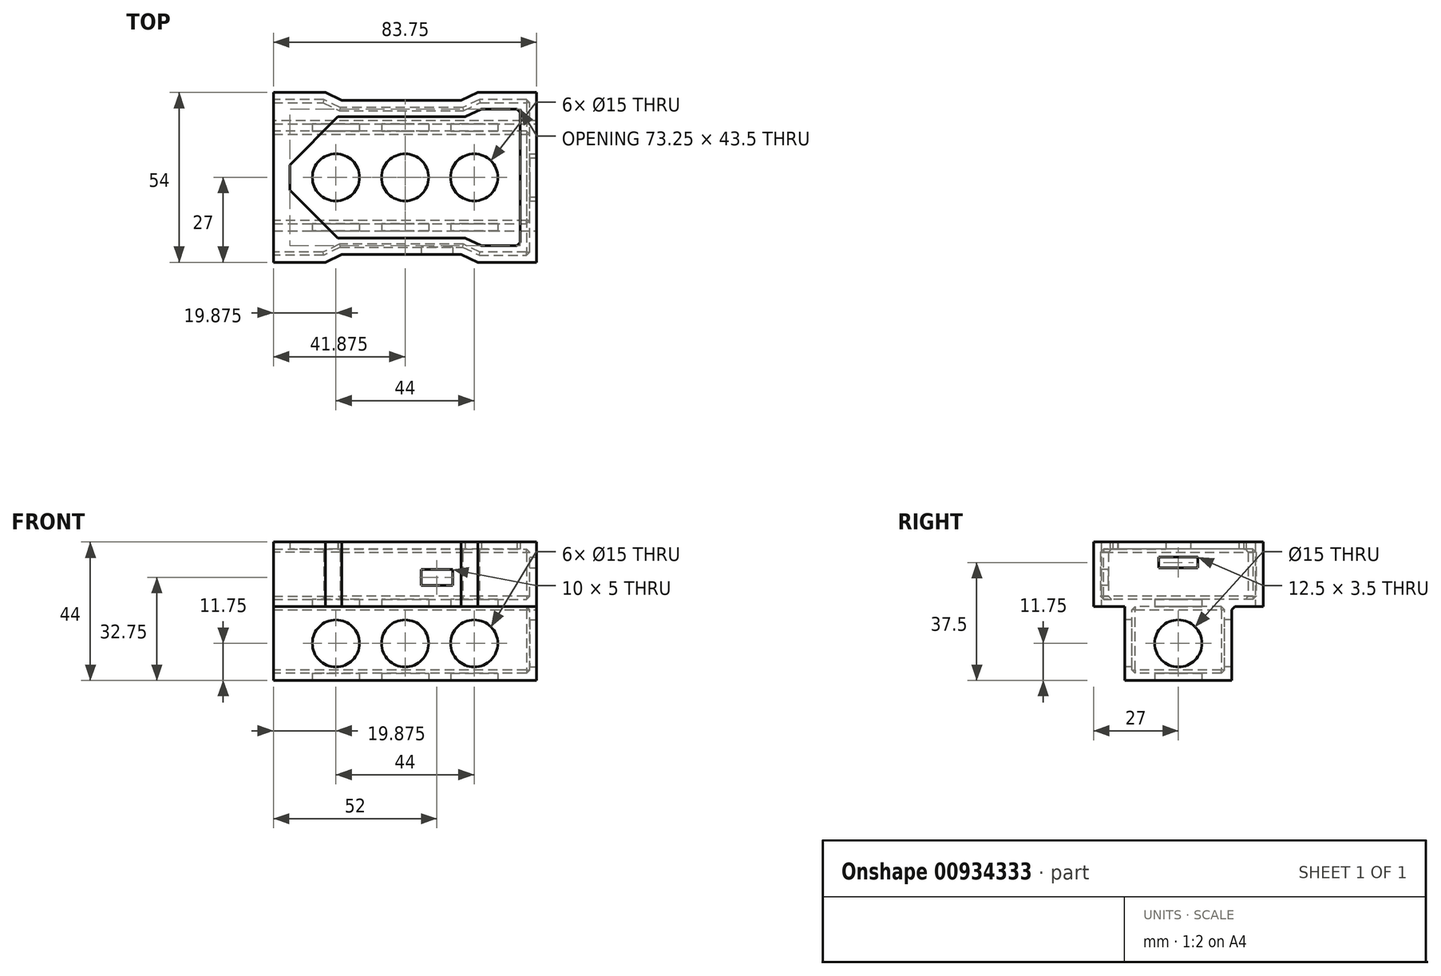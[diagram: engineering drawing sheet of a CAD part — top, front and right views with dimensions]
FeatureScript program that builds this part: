
annotation { "Feature Type Name" : "Feature", "Feature Type Description" : "" }
export const myFeature = defineFeature(function(context is Context, id is Id, definition is map)
    precondition{}
    {
        {
            var Q0;
            Q0=qCreatedBy(makeId("Top.planeOp"),FACE);
            var sketch = newSketch(context, id + "F0", { "sketchPlane" : qUnion([Q0])});
            skLineSegment(sketch, "E0.bottom", {"start": v(0, 0) * mm, "end": v(16, 0) * mm});
            skLineSegment(sketch, "E0.left", {"start": v(0, 0) * mm, "end": v(0, 24.75) * mm});
            skLineSegment(sketch, "E0.right", {"start": v(81.5, 0) * mm, "end": v(81.5, 24.75) * mm});
            skLineSegment(sketch, "E1", {"start": v(16, 0) * mm, "end": v(21.25, 2.5) * mm});
            skLineSegment(sketch, "E2", {"start": v(21.25, 2.5) * mm, "end": v(60.25, 2.5) * mm});
            skLineSegment(sketch, "E3", {"start": v(60.25, 2.5) * mm, "end": v(65.5, 0) * mm});
            skLineSegment(sketch, "E4.trimOffspring", {"start": v(65.5, 0) * mm, "end": v(81.5, 0) * mm});
            skLineSegment(sketch, "E5", {"start": v(0, 24.75) * mm, "end": v(81.5, 24.75) * mm, "construction": true});
            skLineSegment(sketch, "E6.MirrorCS", {"start": v(0, 49.5) * mm, "end": v(0, 24.75) * mm});
            skLineSegment(sketch, "E7.MirrorCS", {"start": v(60.25, 47) * mm, "end": v(65.5, 49.5) * mm});
            skLineSegment(sketch, "E8.MirrorCS", {"start": v(81.5, 49.5) * mm, "end": v(81.5, 24.75) * mm});
            skLineSegment(sketch, "E9.MirrorCS", {"start": v(65.5, 49.5) * mm, "end": v(81.5, 49.5) * mm});
            skLineSegment(sketch, "E10.MirrorCS", {"start": v(16, 49.5) * mm, "end": v(21.25, 47) * mm});
            skLineSegment(sketch, "E11.MirrorCS", {"start": v(21.25, 47) * mm, "end": v(60.25, 47) * mm});
            skLineSegment(sketch, "E12.MirrorCS", {"start": v(0, 49.5) * mm, "end": v(16, 49.5) * mm});
            skSolve(sketch);
        }
        {
            var Q0;
            Q0=makeQuery(id+"F0.imprint","IMPRINT",FACE,{"disambiguationData":[TD([[makeQuery(id+"F0.imprint","IMPRINT",EDGE,{"derivedFrom":sQuery(id+"F0.wireOp",EDGE,"E0.bottom")}),1.0]])]});
            extrude(context, id + "F1", {"entities" : qUnion([Q0]), "depth" : 16 * mm, "offsetDistance" : 25 * mm});
        }
        {
            var Q0;
            Q0=makeQuery(id+"F1.opExtrude","SWEPT_FACE",FACE,{"disambiguationData":[OSD([sQuery(id+"F0.wireOp",EDGE,"E0.left"),sQuery(id+"F0.wireOp",EDGE,"E6.MirrorCS")])]});
            shell(context, id + "F2", {"entities" : qUnion([Q0]), "thickness" : 2.25 * mm, "oppositeDirection" : true});
        }
        {
            var Q0;
            Q0=makeQuery(id+"F1.opExtrude","CAP_FACE",FACE,{"disambiguationData":[OSD([sQuery(id+"F0.wireOp",EDGE,"E0.bottom"),sQuery(id+"F0.wireOp",EDGE,"E0.left"),sQuery(id+"F0.wireOp",EDGE,"E0.right"),sQuery(id+"F0.wireOp",EDGE,"E1"),sQuery(id+"F0.wireOp",EDGE,"E2"),sQuery(id+"F0.wireOp",EDGE,"E3"),sQuery(id+"F0.wireOp",EDGE,"E4.trimOffspring"),sQuery(id+"F0.wireOp",EDGE,"E6.MirrorCS"),sQuery(id+"F0.wireOp",EDGE,"E7.MirrorCS"),sQuery(id+"F0.wireOp",EDGE,"E8.MirrorCS"),sQuery(id+"F0.wireOp",EDGE,"E9.MirrorCS"),sQuery(id+"F0.wireOp",EDGE,"E10.MirrorCS"),sQuery(id+"F0.wireOp",EDGE,"E11.MirrorCS"),sQuery(id+"F0.wireOp",EDGE,"E12.MirrorCS")])],"isStart":true});
            var sketch = newSketch(context, id + "F3", { "sketchPlane" : qUnion([Q0])});
            skLineSegment(sketch, "E13.bottom", {"start": v(0, -7.75) * mm, "end": v(83.75, -7.75) * mm});
            skLineSegment(sketch, "E13.top", {"start": v(0, -41.75) * mm, "end": v(83.75, -41.75) * mm});
            skLineSegment(sketch, "E13.left", {"start": v(0, -7.75) * mm, "end": v(0, -41.75) * mm});
            skLineSegment(sketch, "E13.right", {"start": v(83.75, -7.75) * mm, "end": v(83.75, -41.75) * mm});
            skPoint(sketch, "E14", {"position": v(0, -24.75) * mm});
            skSolve(sketch);
        }
        {
            var Q0;
            Q0 = qSketchRegion(id + "F3", true);
            extrude(context, id + "F4", {"entities" : qUnion([Q0]), "operationType" : NewBodyOperationType.ADD, "depth" : 23.5 * mm, "offsetDistance" : 25 * mm});
        }
        {
            var Q0;
            Q0=makeQuery(id+"F4.boolean.opBoolean","MERGE",FACE,{"derivedFrom":[makeQuery(id+"F1.opExtrude","SWEPT_FACE",FACE,{"disambiguationData":[OSD([sQuery(id+"F0.wireOp",EDGE,"bd4c0ab3-f638-437a-942f-3d293cf75bfd.9"),sQuery(id+"F0.wireOp",EDGE,"bd4c0ab3-f638-437a-942f-3d293cf75bfd.11")])]}),makeQuery(id+"F4.opExtrude","SWEPT_FACE",FACE,{"disambiguationData":[OSD([sQuery(id+"Filse6hUhfh3Ufs_1.wireOp",EDGE,"bbtqiL3y-JQfm-Av7l-CrqV-hF6hky0nlNgT.left")])]})]});
            var Q1;
            Q1=makeQuery(id+"F4.boolean.opBoolean","MERGE",FACE,{"derivedFrom":[makeQuery(id+"F1.opExtrude","SWEPT_FACE",FACE,{"disambiguationData":[OSD([sQuery(id+"F0.wireOp",EDGE,"E0.left"),sQuery(id+"F0.wireOp",EDGE,"E6.MirrorCS")])]}),makeQuery(id+"F4.opExtrude","SWEPT_FACE",FACE,{"disambiguationData":[OSD([sQuery(id+"F3.wireOp",EDGE,"E13.left")])]})]});
            var Q2;
            Q2=makeQuery(id+"F1.opExtrude","SWEPT_BODY",BODY,{"disambiguationData":[OSD([sQuery(id+"F0.wireOp",EDGE,"E0.bottom"),sQuery(id+"F0.wireOp",EDGE,"E0.left"),sQuery(id+"F0.wireOp",EDGE,"E0.right"),sQuery(id+"F0.wireOp",EDGE,"E1"),sQuery(id+"F0.wireOp",EDGE,"E2"),sQuery(id+"F0.wireOp",EDGE,"E3"),sQuery(id+"F0.wireOp",EDGE,"E4.trimOffspring"),sQuery(id+"F0.wireOp",EDGE,"E6.MirrorCS"),sQuery(id+"F0.wireOp",EDGE,"E7.MirrorCS"),sQuery(id+"F0.wireOp",EDGE,"E8.MirrorCS"),sQuery(id+"F0.wireOp",EDGE,"E9.MirrorCS"),sQuery(id+"F0.wireOp",EDGE,"E10.MirrorCS"),sQuery(id+"F0.wireOp",EDGE,"E11.MirrorCS"),sQuery(id+"F0.wireOp",EDGE,"E12.MirrorCS")])]});
            shell(context, id + "F5", {"entities" : qUnion([Q0, Q1]), "parts" : qUnion([Q2]), "thickness" : 2.25 * mm});
        }
        {
            var Q0;
            {var subQ0=sQuery(id+"F0.wireOp",EDGE,"E12.MirrorCS");var subQ1=sQuery(id+"F0.wireOp",EDGE,"E11.MirrorCS");var subQ2=sQuery(id+"F0.wireOp",EDGE,"E10.MirrorCS");var subQ3=sQuery(id+"F0.wireOp",EDGE,"E9.MirrorCS");var subQ4=sQuery(id+"F0.wireOp",EDGE,"E8.MirrorCS");var subQ5=sQuery(id+"F0.wireOp",EDGE,"E7.MirrorCS");var subQ6=sQuery(id+"F0.wireOp",EDGE,"E6.MirrorCS");var subQ7=sQuery(id+"F0.wireOp",EDGE,"E4.trimOffspring");var subQ8=sQuery(id+"F0.wireOp",EDGE,"E3");var subQ9=sQuery(id+"F0.wireOp",EDGE,"E2");var subQ10=sQuery(id+"F0.wireOp",EDGE,"E1");var subQ11=sQuery(id+"F0.wireOp",EDGE,"E0.right");var subQ12=sQuery(id+"F0.wireOp",EDGE,"E0.left");var subQ13=sQuery(id+"F0.wireOp",EDGE,"E0.bottom");Q0=makeQuery(id+"F2.opShell","OFFSET_FACE",FACE,{"disambiguationData":[OSD([subQ13,subQ12,subQ11,subQ10,subQ9,subQ8,subQ7,subQ6,subQ5,subQ4,subQ3,subQ2,subQ1,subQ0]),TDD([makeQuery(id+"F1.opExtrude","CAP_FACE",FACE,{"disambiguationData":[OSD([subQ13,subQ12,subQ11,subQ10,subQ9,subQ8,subQ7,subQ6,subQ5,subQ4,subQ3,subQ2,subQ1,subQ0])],"isStart":false})])]});}
            var Q1;
            Q1=makeQuery(id+"F1.opExtrude","CAP_FACE",FACE,{"disambiguationData":[OSD([sQuery(id+"F0.wireOp",EDGE,"E0.bottom"),sQuery(id+"F0.wireOp",EDGE,"E0.left"),sQuery(id+"F0.wireOp",EDGE,"E0.right"),sQuery(id+"F0.wireOp",EDGE,"E1"),sQuery(id+"F0.wireOp",EDGE,"E2"),sQuery(id+"F0.wireOp",EDGE,"E3"),sQuery(id+"F0.wireOp",EDGE,"E4.trimOffspring"),sQuery(id+"F0.wireOp",EDGE,"E6.MirrorCS"),sQuery(id+"F0.wireOp",EDGE,"E7.MirrorCS"),sQuery(id+"F0.wireOp",EDGE,"E8.MirrorCS"),sQuery(id+"F0.wireOp",EDGE,"E9.MirrorCS"),sQuery(id+"F0.wireOp",EDGE,"E10.MirrorCS"),sQuery(id+"F0.wireOp",EDGE,"E11.MirrorCS"),sQuery(id+"F0.wireOp",EDGE,"E12.MirrorCS")])],"isStart":false});
            shell(context, id + "F6", {"entities" : qUnion([Q0, Q1]), "thickness" : 5.25 * mm});
        }
        {
            var Q0;
            Q0=makeQuery(id+"F6.opShell","OFFSET_EDGE",EDGE,{"disambiguationData":[OSD([sQuery(id+"F0.wireOp",EDGE,"E6.MirrorCS"),sQuery(id+"F0.wireOp",EDGE,"E12.MirrorCS")])]});
            var Q1;
            Q1=makeQuery(id+"F6.opShell","OFFSET_EDGE",EDGE,{"disambiguationData":[OSD([sQuery(id+"F0.wireOp",EDGE,"E0.bottom"),sQuery(id+"F0.wireOp",EDGE,"E0.left")])]});
            chamfer(context, id + "F7", {"entities" : qUnion([Q0, Q1]), "width" : 17.75 * mm, "tangentPropagation" : true});
        }
        {
            var Q0;
            Q0=makeQuery(id+"F4.boolean.opBoolean","MERGE",FACE,{"derivedFrom":[makeQuery(id+"F1.opExtrude","SWEPT_FACE",FACE,{"disambiguationData":[OSD([sQuery(id+"F0.wireOp",EDGE,"E0.right"),sQuery(id+"F0.wireOp",EDGE,"E8.MirrorCS")])]}),makeQuery(id+"F4.opExtrude","SWEPT_FACE",FACE,{"disambiguationData":[OSD([sQuery(id+"F3.wireOp",EDGE,"E13.right")])]})]});
            var sketch = newSketch(context, id + "F8", { "sketchPlane" : qUnion([Q0])});
            skPoint(sketch, "E15", {"position": v(24.75, -14) * mm});
            skPoint(sketch, "E16", {"position": v(27.14, 12.96) * mm});
            skPoint(sketch, "E17", {"position": v(-220.52, 60.4) * mm});
            skPoint(sketch, "E18", {"position": v(-318.2, 70.36) * mm});
            skSolve(sketch);
        }
        {
            var Q0;
            Q0=makeQuery(id+"F4.opExtrude","SWEPT_FACE",FACE,{"disambiguationData":[OSD([sQuery(id+"F3.wireOp",EDGE,"E13.bottom")])]});
            var sketch = newSketch(context, id + "F9", { "sketchPlane" : qUnion([Q0])});
            skPoint(sketch, "E19", {"position": v(41.88, -14) * mm});
            skPoint(sketch, "E20", {"position": v(19.88, -14) * mm});
            skPoint(sketch, "E21", {"position": v(63.88, -14) * mm});
            skSolve(sketch);
        }
        {
            var Q0;
            Q0=makeQuery(id+"F4.opExtrude","CAP_FACE",FACE,{"disambiguationData":[OSD([sQuery(id+"F3.wireOp",EDGE,"E13.bottom"),sQuery(id+"F3.wireOp",EDGE,"E13.top"),sQuery(id+"F3.wireOp",EDGE,"E13.left"),sQuery(id+"F3.wireOp",EDGE,"E13.right")])],"isStart":false});
            var sketch = newSketch(context, id + "F10", { "sketchPlane" : qUnion([Q0])});
            skPoint(sketch, "E22", {"position": v(63.88, -24.75) * mm});
            skPoint(sketch, "E22.positionSnap0", {"position": v(83.75, -24.75) * mm});
            skPoint(sketch, "E23", {"position": v(41.88, -24.75) * mm});
            skPoint(sketch, "E24", {"position": v(19.88, -24.75) * mm});
            skSolve(sketch);
        }
        {
            var Q0;
            Q0=sQuery(id+"F8.wireOp",VERTEX,"E15");
            var Q1;
            Q1=sQuery(id+"F9.wireOp",VERTEX,"E19");
            var Q2;
            Q2=sQuery(id+"F9.wireOp",VERTEX,"E20");
            var Q3;
            Q3=sQuery(id+"F9.wireOp",VERTEX,"E21");
            var Q4;
            Q4=sQuery(id+"F10.wireOp",VERTEX,"E24");
            var Q5;
            Q5=sQuery(id+"F10.wireOp",VERTEX,"E23");
            var Q6;
            Q6=sQuery(id+"F10.wireOp",VERTEX,"E22");
            var Q7;
            Q7=makeQuery(id+"F1.opExtrude","SWEPT_BODY",BODY,{"disambiguationData":[OSD([sQuery(id+"F0.wireOp",EDGE,"E0.bottom"),sQuery(id+"F0.wireOp",EDGE,"E0.left"),sQuery(id+"F0.wireOp",EDGE,"E0.right"),sQuery(id+"F0.wireOp",EDGE,"E1"),sQuery(id+"F0.wireOp",EDGE,"E2"),sQuery(id+"F0.wireOp",EDGE,"E3"),sQuery(id+"F0.wireOp",EDGE,"E4.trimOffspring"),sQuery(id+"F0.wireOp",EDGE,"E6.MirrorCS"),sQuery(id+"F0.wireOp",EDGE,"E7.MirrorCS"),sQuery(id+"F0.wireOp",EDGE,"E8.MirrorCS"),sQuery(id+"F0.wireOp",EDGE,"E9.MirrorCS"),sQuery(id+"F0.wireOp",EDGE,"E10.MirrorCS"),sQuery(id+"F0.wireOp",EDGE,"E11.MirrorCS"),sQuery(id+"F0.wireOp",EDGE,"E12.MirrorCS")])]});
            hole(context, id + "F11", {"style" : HoleStyle.SIMPLE, "endStyle" : HoleEndStyle.BLIND, "holeDiameter" : 15 * mm, "majorDiameter" : 5 * mm, "holeDepth" : 300 * mm, "isTappedThrough" : true, "tappedDepth" : 12 * mm, "tapClearance" : 3, "startFromSketch" : true, "locations" : qUnion([Q0, Q1, Q2, Q3, Q4, Q5, Q6]), "scope" : qUnion([Q7])});
        }
        {
            var Q0;
            {var subQ0=sQuery(id+"F3.wireOp",EDGE,"E13.right");Q0=makeQuery(id+"F8.imprint","IMPRINT",FACE,{"disambiguationData":[TD([[makeQuery(id+"F8.imprint","IMPRINT",EDGE,{"derivedFrom":makeQuery(id+"F4.opExtrude","CAP_EDGE",EDGE,{"disambiguationData":[OSD([subQ0])],"isStart":false})}),1.0]])]});}
            var sketch = newSketch(context, id + "F12", { "sketchPlane" : qUnion([Q0])});
            skLineSegment(sketch, "E25.bottom", {"start": v(18.5, 13.5) * mm, "end": v(31, 13.5) * mm});
            skLineSegment(sketch, "E25.top", {"start": v(18.5, 10) * mm, "end": v(31, 10) * mm});
            skLineSegment(sketch, "E25.left", {"start": v(18.5, 13.5) * mm, "end": v(18.5, 10) * mm});
            skLineSegment(sketch, "E25.right", {"start": v(31, 13.5) * mm, "end": v(31, 10) * mm});
            skPoint(sketch, "E26", {"position": v(24.75, 13.5) * mm});
            skSolve(sketch);
        }
        {
            var Q0;
            Q0 = qSketchRegion(id + "F12", true);
            extrude(context, id + "F13", {"entities" : qUnion([Q0]), "operationType" : NewBodyOperationType.REMOVE, "oppositeDirection" : true, "depth" : 25 * mm, "offsetDistance" : 25 * mm});
        }
        {
            var Q0;
            Q0=makeQuery(id+"F1.opExtrude","SWEPT_FACE",FACE,{"disambiguationData":[OSD([sQuery(id+"F0.wireOp",EDGE,"E2")])]});
            var sketch = newSketch(context, id + "F14", { "sketchPlane" : qUnion([Q0])});
            skLineSegment(sketch, "E27.bottom", {"start": v(47, 9.5) * mm, "end": v(57, 9.5) * mm});
            skLineSegment(sketch, "E27.top", {"start": v(47, 4.5) * mm, "end": v(57, 4.5) * mm});
            skLineSegment(sketch, "E27.left", {"start": v(47, 9.5) * mm, "end": v(47, 4.5) * mm});
            skLineSegment(sketch, "E27.right", {"start": v(57, 9.5) * mm, "end": v(57, 4.5) * mm});
            skSolve(sketch);
        }
        {
            var Q0;
            Q0 = qSketchRegion(id + "F14", true);
            extrude(context, id + "F15", {"entities" : qUnion([Q0]), "operationType" : NewBodyOperationType.REMOVE, "oppositeDirection" : true, "depth" : 25 * mm, "offsetDistance" : 25 * mm});
        }
        {
            var Q0;
            Q0=makeQuery(id+"F5.opShell","OFFSET_EDGE",EDGE,{"disambiguationData":[OSD([sQuery(id+"F3.wireOp",EDGE,"E13.top")])]});
            var Q1;
            Q1=makeQuery(id+"F5.opShell","OFFSET_EDGE",EDGE,{"disambiguationData":[OSD([sQuery(id+"F3.wireOp",EDGE,"E13.bottom")])]});
            var Q2;
            Q2=makeQuery(id+"F4.opExtrude","CAP_EDGE",EDGE,{"disambiguationData":[OSD([sQuery(id+"F3.wireOp",EDGE,"E13.top")])],"isStart":true});
            var Q3;
            Q3=makeQuery(id+"F4.opExtrude","CAP_EDGE",EDGE,{"disambiguationData":[OSD([sQuery(id+"F3.wireOp",EDGE,"E13.bottom")])],"isStart":true});
            var Q4;
            Q4=makeQuery(id+"F5.opShell","OFFSET_EDGE",EDGE,{"disambiguationData":[OSD([sQuery(id+"F3.wireOp",EDGE,"E13.right")])]});
            var Q5;
            Q5=makeQuery(id+"F5.opShell","OFFSET_EDGE",EDGE,{"disambiguationData":[OSD([sQuery(id+"F0.wireOp",EDGE,"E0.right"),sQuery(id+"F0.wireOp",EDGE,"E8.MirrorCS"),sQuery(id+"F3.wireOp",EDGE,"E13.bottom"),sQuery(id+"F3.wireOp",EDGE,"E13.right")])]});
            var Q6;
            Q6=makeQuery(id+"F5.opShell","OFFSET_EDGE",EDGE,{"disambiguationData":[OSD([sQuery(id+"F0.wireOp",EDGE,"E0.right"),sQuery(id+"F0.wireOp",EDGE,"E8.MirrorCS"),sQuery(id+"F3.wireOp",EDGE,"E13.top"),sQuery(id+"F3.wireOp",EDGE,"E13.right")])]});
            var Q7;
            {var subQ0=sQuery(id+"F0.wireOp",EDGE,"E12.MirrorCS");var subQ1=sQuery(id+"F0.wireOp",EDGE,"E11.MirrorCS");var subQ2=sQuery(id+"F0.wireOp",EDGE,"E10.MirrorCS");var subQ3=sQuery(id+"F0.wireOp",EDGE,"E9.MirrorCS");var subQ4=sQuery(id+"F0.wireOp",EDGE,"E8.MirrorCS");var subQ5=sQuery(id+"F0.wireOp",EDGE,"E7.MirrorCS");var subQ6=sQuery(id+"F0.wireOp",EDGE,"E6.MirrorCS");var subQ7=sQuery(id+"F0.wireOp",EDGE,"E4.trimOffspring");var subQ8=sQuery(id+"F0.wireOp",EDGE,"E3");var subQ9=sQuery(id+"F0.wireOp",EDGE,"E2");var subQ10=sQuery(id+"F0.wireOp",EDGE,"E1");var subQ11=sQuery(id+"F0.wireOp",EDGE,"E0.right");var subQ12=sQuery(id+"F0.wireOp",EDGE,"E0.left");var subQ13=sQuery(id+"F0.wireOp",EDGE,"E0.bottom");Q7=makeQuery(id+"F5.opShell","TWEAK_EDGE",EDGE,{"derivedFrom":[makeQuery(id+"F2.opShell","OFFSET_FACE",FACE,{"disambiguationData":[OSD([subQ13,subQ12,subQ11,subQ10,subQ9,subQ8,subQ7,subQ6,subQ5,subQ4,subQ3,subQ2,subQ1,subQ0]),TDD([makeQuery(id+"F1.opExtrude","CAP_FACE",FACE,{"disambiguationData":[OSD([subQ13,subQ12,subQ11,subQ10,subQ9,subQ8,subQ7,subQ6,subQ5,subQ4,subQ3,subQ2,subQ1,subQ0])],"isStart":true})])]}),makeQuery(id+"F4.opExtrude","SWEPT_FACE",FACE,{"disambiguationData":[OSD([sQuery(id+"F3.wireOp",EDGE,"E13.top")])]})]});}
            var Q8;
            {var subQ0=sQuery(id+"F0.wireOp",EDGE,"E8.MirrorCS");var subQ1=sQuery(id+"F0.wireOp",EDGE,"E0.right");var subQ2=sQuery(id+"F0.wireOp",EDGE,"E12.MirrorCS");var subQ3=sQuery(id+"F0.wireOp",EDGE,"E11.MirrorCS");var subQ4=sQuery(id+"F0.wireOp",EDGE,"E10.MirrorCS");var subQ5=sQuery(id+"F0.wireOp",EDGE,"E9.MirrorCS");var subQ6=sQuery(id+"F0.wireOp",EDGE,"E7.MirrorCS");var subQ7=sQuery(id+"F0.wireOp",EDGE,"E6.MirrorCS");var subQ8=sQuery(id+"F0.wireOp",EDGE,"E4.trimOffspring");var subQ9=sQuery(id+"F0.wireOp",EDGE,"E3");var subQ10=sQuery(id+"F0.wireOp",EDGE,"E2");var subQ11=sQuery(id+"F0.wireOp",EDGE,"E1");var subQ12=sQuery(id+"F0.wireOp",EDGE,"E0.left");var subQ13=sQuery(id+"F0.wireOp",EDGE,"E0.bottom");Q8=makeQuery(id+"F5.opShell","TWEAK_EDGE",EDGE,{"derivedFrom":[makeQuery(id+"F2.opShell","OFFSET_FACE",FACE,{"disambiguationData":[OSD([subQ13,subQ12,subQ1,subQ11,subQ10,subQ9,subQ8,subQ7,subQ6,subQ0,subQ5,subQ4,subQ3,subQ2]),TDD([makeQuery(id+"F1.opExtrude","CAP_FACE",FACE,{"disambiguationData":[OSD([subQ13,subQ12,subQ1,subQ11,subQ10,subQ9,subQ8,subQ7,subQ6,subQ0,subQ5,subQ4,subQ3,subQ2])],"isStart":true})])]}),makeQuery(id+"F4.boolean.opBoolean","MERGE",FACE,{"derivedFrom":[makeQuery(id+"F1.opExtrude","SWEPT_FACE",FACE,{"disambiguationData":[OSD([subQ1,subQ0])]}),makeQuery(id+"F4.opExtrude","SWEPT_FACE",FACE,{"disambiguationData":[OSD([sQuery(id+"F3.wireOp",EDGE,"E13.right")])]})]})]});}
            var Q9;
            {var subQ0=sQuery(id+"F0.wireOp",EDGE,"E12.MirrorCS");var subQ1=sQuery(id+"F0.wireOp",EDGE,"E11.MirrorCS");var subQ2=sQuery(id+"F0.wireOp",EDGE,"E10.MirrorCS");var subQ3=sQuery(id+"F0.wireOp",EDGE,"E9.MirrorCS");var subQ4=sQuery(id+"F0.wireOp",EDGE,"E8.MirrorCS");var subQ5=sQuery(id+"F0.wireOp",EDGE,"E7.MirrorCS");var subQ6=sQuery(id+"F0.wireOp",EDGE,"E6.MirrorCS");var subQ7=sQuery(id+"F0.wireOp",EDGE,"E4.trimOffspring");var subQ8=sQuery(id+"F0.wireOp",EDGE,"E3");var subQ9=sQuery(id+"F0.wireOp",EDGE,"E2");var subQ10=sQuery(id+"F0.wireOp",EDGE,"E1");var subQ11=sQuery(id+"F0.wireOp",EDGE,"E0.right");var subQ12=sQuery(id+"F0.wireOp",EDGE,"E0.left");var subQ13=sQuery(id+"F0.wireOp",EDGE,"E0.bottom");Q9=makeQuery(id+"F5.opShell","TWEAK_EDGE",EDGE,{"derivedFrom":[makeQuery(id+"F2.opShell","OFFSET_FACE",FACE,{"disambiguationData":[OSD([subQ13,subQ12,subQ11,subQ10,subQ9,subQ8,subQ7,subQ6,subQ5,subQ4,subQ3,subQ2,subQ1,subQ0]),TDD([makeQuery(id+"F1.opExtrude","CAP_FACE",FACE,{"disambiguationData":[OSD([subQ13,subQ12,subQ11,subQ10,subQ9,subQ8,subQ7,subQ6,subQ5,subQ4,subQ3,subQ2,subQ1,subQ0])],"isStart":true})])]}),makeQuery(id+"F4.opExtrude","SWEPT_FACE",FACE,{"disambiguationData":[OSD([sQuery(id+"F3.wireOp",EDGE,"E13.bottom")])]})]});}
            var Q10;
            {var subQ0=sQuery(id+"F0.wireOp",EDGE,"E12.MirrorCS");Q10=makeQuery(id+"F2.opShell","OFFSET_EDGE",EDGE,{"disambiguationData":[OSD([subQ0]),TDD([makeQuery(id+"F1.opExtrude","CAP_EDGE",EDGE,{"disambiguationData":[OSD([subQ0])],"isStart":true})])]});}
            var Q11;
            {var subQ0=sQuery(id+"F0.wireOp",EDGE,"E10.MirrorCS");Q11=makeQuery(id+"F2.opShell","OFFSET_EDGE",EDGE,{"disambiguationData":[OSD([subQ0]),TDD([makeQuery(id+"F1.opExtrude","CAP_EDGE",EDGE,{"disambiguationData":[OSD([subQ0])],"isStart":true})])]});}
            var Q12;
            {var subQ0=sQuery(id+"F0.wireOp",EDGE,"E11.MirrorCS");Q12=makeQuery(id+"F2.opShell","OFFSET_EDGE",EDGE,{"disambiguationData":[OSD([subQ0]),TDD([makeQuery(id+"F1.opExtrude","CAP_EDGE",EDGE,{"disambiguationData":[OSD([subQ0])],"isStart":true})])]});}
            var Q13;
            {var subQ0=sQuery(id+"F0.wireOp",EDGE,"E7.MirrorCS");Q13=makeQuery(id+"F2.opShell","OFFSET_EDGE",EDGE,{"disambiguationData":[OSD([subQ0]),TDD([makeQuery(id+"F1.opExtrude","CAP_EDGE",EDGE,{"disambiguationData":[OSD([subQ0])],"isStart":true})])]});}
            var Q14;
            {var subQ0=sQuery(id+"F0.wireOp",EDGE,"E9.MirrorCS");Q14=makeQuery(id+"F2.opShell","OFFSET_EDGE",EDGE,{"disambiguationData":[OSD([subQ0]),TDD([makeQuery(id+"F1.opExtrude","CAP_EDGE",EDGE,{"disambiguationData":[OSD([subQ0])],"isStart":true})])]});}
            var Q15;
            Q15=makeQuery(id+"F2.opShell","OFFSET_EDGE",EDGE,{"disambiguationData":[OSD([sQuery(id+"F0.wireOp",EDGE,"E8.MirrorCS"),sQuery(id+"F0.wireOp",EDGE,"E9.MirrorCS")])]});
            var Q16;
            {var subQ0=sQuery(id+"F0.wireOp",EDGE,"E8.MirrorCS");var subQ1=sQuery(id+"F0.wireOp",EDGE,"E0.right");Q16=makeQuery(id+"F2.opShell","OFFSET_EDGE",EDGE,{"disambiguationData":[OSD([subQ1,subQ0]),TDD([makeQuery(id+"F1.opExtrude","CAP_EDGE",EDGE,{"disambiguationData":[OSD([subQ1,subQ0])],"isStart":true})])]});}
            var Q17;
            {var subQ0=sQuery(id+"F0.wireOp",EDGE,"E4.trimOffspring");Q17=makeQuery(id+"F2.opShell","OFFSET_EDGE",EDGE,{"disambiguationData":[OSD([subQ0]),TDD([makeQuery(id+"F1.opExtrude","CAP_EDGE",EDGE,{"disambiguationData":[OSD([subQ0])],"isStart":true})])]});}
            var Q18;
            {var subQ0=sQuery(id+"F0.wireOp",EDGE,"E3");Q18=makeQuery(id+"F2.opShell","OFFSET_EDGE",EDGE,{"disambiguationData":[OSD([subQ0]),TDD([makeQuery(id+"F1.opExtrude","CAP_EDGE",EDGE,{"disambiguationData":[OSD([subQ0])],"isStart":true})])]});}
            var Q19;
            {var subQ0=sQuery(id+"F0.wireOp",EDGE,"E2");Q19=makeQuery(id+"F2.opShell","OFFSET_EDGE",EDGE,{"disambiguationData":[OSD([subQ0]),TDD([makeQuery(id+"F1.opExtrude","CAP_EDGE",EDGE,{"disambiguationData":[OSD([subQ0])],"isStart":true})])]});}
            var Q20;
            Q20=makeQuery(id+"F2.opShell","OFFSET_EDGE",EDGE,{"disambiguationData":[OSD([sQuery(id+"F0.wireOp",EDGE,"E0.right"),sQuery(id+"F0.wireOp",EDGE,"E4.trimOffspring")])]});
            var Q21;
            {var subQ0=sQuery(id+"F0.wireOp",EDGE,"E0.bottom");Q21=makeQuery(id+"F2.opShell","OFFSET_EDGE",EDGE,{"disambiguationData":[OSD([subQ0]),TDD([makeQuery(id+"F1.opExtrude","CAP_EDGE",EDGE,{"disambiguationData":[OSD([subQ0])],"isStart":true})])]});}
            var Q22;
            {var subQ0=sQuery(id+"F0.wireOp",EDGE,"E1");Q22=makeQuery(id+"F2.opShell","OFFSET_EDGE",EDGE,{"disambiguationData":[OSD([subQ0]),TDD([makeQuery(id+"F1.opExtrude","CAP_EDGE",EDGE,{"disambiguationData":[OSD([subQ0])],"isStart":true})])]});}
            var Q23;
            {var subQ0=sQuery(id+"F0.wireOp",EDGE,"E12.MirrorCS");Q23=makeQuery(id+"F2.opShell","OFFSET_EDGE",EDGE,{"disambiguationData":[OSD([subQ0]),TDD([makeQuery(id+"F1.opExtrude","CAP_EDGE",EDGE,{"disambiguationData":[OSD([subQ0])],"isStart":false})])]});}
            var Q24;
            {var subQ0=sQuery(id+"F0.wireOp",EDGE,"E10.MirrorCS");Q24=makeQuery(id+"F2.opShell","OFFSET_EDGE",EDGE,{"disambiguationData":[OSD([subQ0]),TDD([makeQuery(id+"F1.opExtrude","CAP_EDGE",EDGE,{"disambiguationData":[OSD([subQ0])],"isStart":false})])]});}
            var Q25;
            {var subQ0=sQuery(id+"F0.wireOp",EDGE,"E11.MirrorCS");Q25=makeQuery(id+"F2.opShell","OFFSET_EDGE",EDGE,{"disambiguationData":[OSD([subQ0]),TDD([makeQuery(id+"F1.opExtrude","CAP_EDGE",EDGE,{"disambiguationData":[OSD([subQ0])],"isStart":false})])]});}
            var Q26;
            {var subQ0=sQuery(id+"F0.wireOp",EDGE,"E9.MirrorCS");Q26=makeQuery(id+"F2.opShell","OFFSET_EDGE",EDGE,{"disambiguationData":[OSD([subQ0]),TDD([makeQuery(id+"F1.opExtrude","CAP_EDGE",EDGE,{"disambiguationData":[OSD([subQ0])],"isStart":false})])]});}
            var Q27;
            {var subQ0=sQuery(id+"F0.wireOp",EDGE,"E8.MirrorCS");var subQ1=sQuery(id+"F0.wireOp",EDGE,"E0.right");Q27=makeQuery(id+"F2.opShell","OFFSET_EDGE",EDGE,{"disambiguationData":[OSD([subQ1,subQ0]),TDD([makeQuery(id+"F1.opExtrude","CAP_EDGE",EDGE,{"disambiguationData":[OSD([subQ1,subQ0])],"isStart":false})])]});}
            var Q28;
            {var subQ0=sQuery(id+"F0.wireOp",EDGE,"E0.bottom");Q28=makeQuery(id+"F2.opShell","OFFSET_EDGE",EDGE,{"disambiguationData":[OSD([subQ0]),TDD([makeQuery(id+"F1.opExtrude","CAP_EDGE",EDGE,{"disambiguationData":[OSD([subQ0])],"isStart":false})])]});}
            var Q29;
            {var subQ0=sQuery(id+"F0.wireOp",EDGE,"E1");Q29=makeQuery(id+"F2.opShell","OFFSET_EDGE",EDGE,{"disambiguationData":[OSD([subQ0]),TDD([makeQuery(id+"F1.opExtrude","CAP_EDGE",EDGE,{"disambiguationData":[OSD([subQ0])],"isStart":false})])]});}
            var Q30;
            {var subQ0=sQuery(id+"F0.wireOp",EDGE,"E2");Q30=makeQuery(id+"F2.opShell","OFFSET_EDGE",EDGE,{"disambiguationData":[OSD([subQ0]),TDD([makeQuery(id+"F1.opExtrude","CAP_EDGE",EDGE,{"disambiguationData":[OSD([subQ0])],"isStart":false})])]});}
            var Q31;
            {var subQ0=sQuery(id+"F0.wireOp",EDGE,"E4.trimOffspring");Q31=makeQuery(id+"F2.opShell","OFFSET_EDGE",EDGE,{"disambiguationData":[OSD([subQ0]),TDD([makeQuery(id+"F1.opExtrude","CAP_EDGE",EDGE,{"disambiguationData":[OSD([subQ0])],"isStart":false})])]});}
            var Q32;
            Q32=makeQuery(id+"F6.opShell","OFFSET_EDGE",EDGE,{"disambiguationData":[OSD([sQuery(id+"F0.wireOp",EDGE,"E0.right"),sQuery(id+"F0.wireOp",EDGE,"E4.trimOffspring")])]});
            var Q33;
            Q33=makeQuery(id+"F6.opShell","OFFSET_EDGE",EDGE,{"disambiguationData":[OSD([sQuery(id+"F0.wireOp",EDGE,"E8.MirrorCS"),sQuery(id+"F0.wireOp",EDGE,"E9.MirrorCS")])]});
            var Q34;
            {var subQ0=sQuery(id+"F0.wireOp",EDGE,"E7.MirrorCS");Q34=makeQuery(id+"F2.opShell","OFFSET_EDGE",EDGE,{"disambiguationData":[OSD([subQ0]),TDD([makeQuery(id+"F1.opExtrude","CAP_EDGE",EDGE,{"disambiguationData":[OSD([subQ0])],"isStart":false})])]});}
            var Q35;
            {var subQ0=sQuery(id+"F0.wireOp",EDGE,"E3");Q35=makeQuery(id+"F2.opShell","OFFSET_EDGE",EDGE,{"disambiguationData":[OSD([subQ0]),TDD([makeQuery(id+"F1.opExtrude","CAP_EDGE",EDGE,{"disambiguationData":[OSD([subQ0])],"isStart":false})])]});}
            chamfer(context, id + "F16", {"entities" : qUnion([Q0, Q1, Q2, Q3, Q4, Q5, Q6, Q7, Q8, Q9, Q10, Q11, Q12, Q13, Q14, Q15, Q16, Q17, Q18, Q19, Q20, Q21, Q22, Q23, Q24, Q25, Q26, Q27, Q28, Q29, Q30, Q31, Q32, Q33, Q34, Q35]), "width" : 1 * mm, "tangentPropagation" : true});
        }
    });
